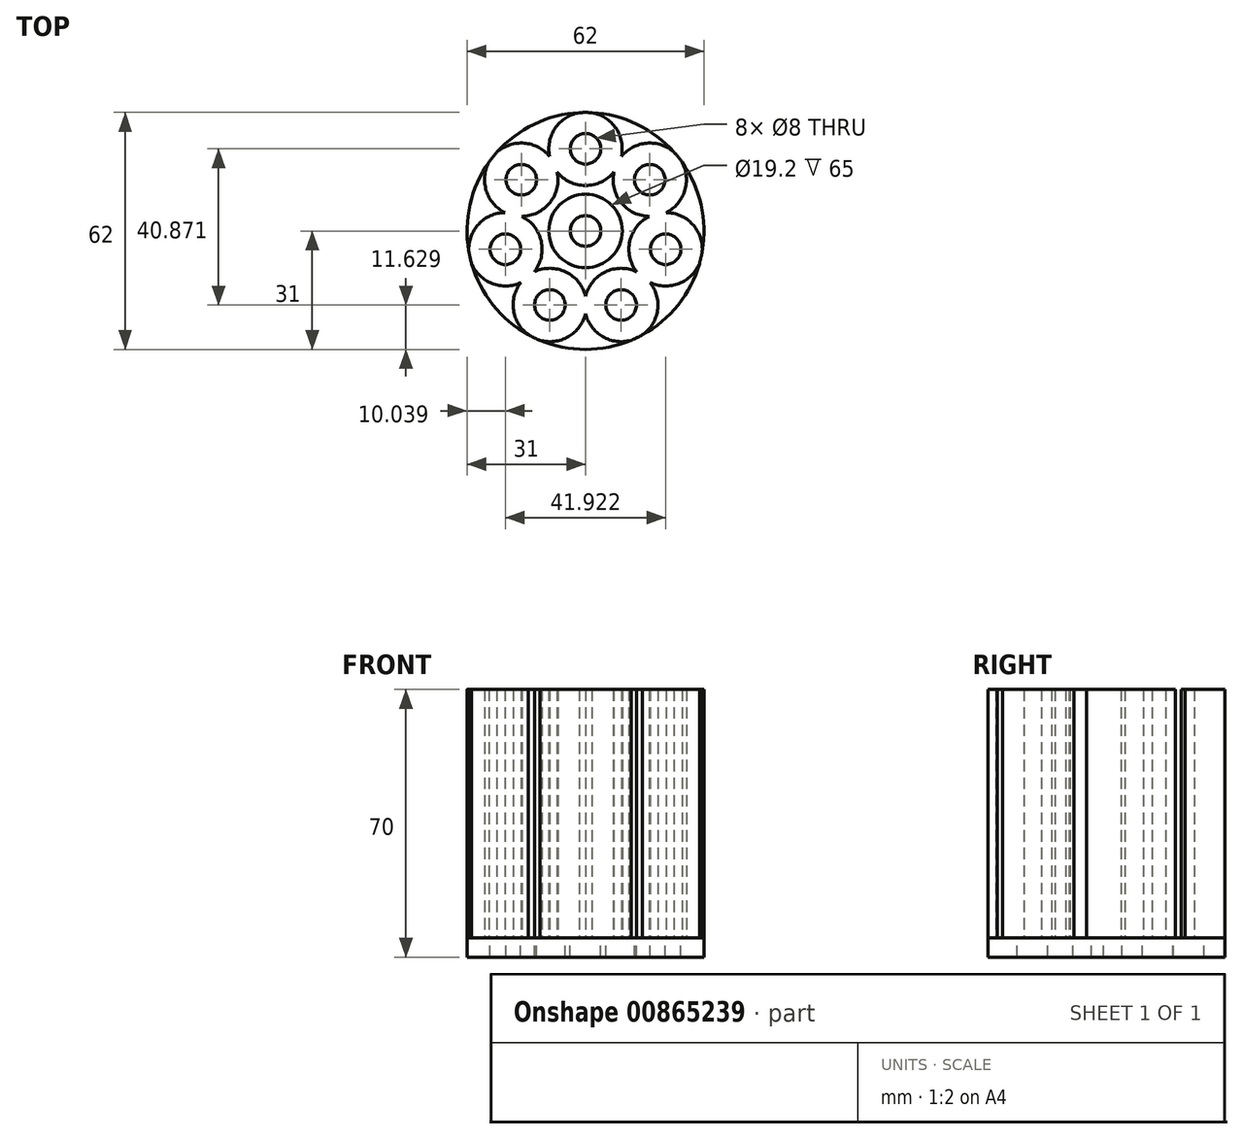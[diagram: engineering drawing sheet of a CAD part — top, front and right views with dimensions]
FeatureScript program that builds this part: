
annotation { "Feature Type Name" : "Feature", "Feature Type Description" : "" }
export const myFeature = defineFeature(function(context is Context, id is Id, definition is map)
    precondition{}
    {
        {
            var Q0;
            Q0=qCreatedBy(makeId("Top.planeOp"),FACE);
            var sketch = newSketch(context, id + "F0", { "sketchPlane" : qUnion([Q0])});
            skArc(sketch, "E0", {"start": v(-11.94, -28.6) * mm, "mid": v(0, -31) * mm, "end": v(11.94, -28.6) * mm});
            skArc(sketch, "E1", {"start": v(-7.42, 15.41) * mm, "mid": v(0, 11.9) * mm, "end": v(7.42, 15.41) * mm});
            skArc(sketch, "E2.1.0", {"start": v(-9.39, 19.5) * mm, "mid": v(-16.04, 22.97) * mm, "end": v(-23.17, 20.6) * mm});
            skArc(sketch, "E2.2.0", {"start": v(-21.1, 4.81) * mm, "mid": v(-27.97, 1.78) * mm, "end": v(-30.55, -5.27) * mm});
            skArc(sketch, "E2.3.0", {"start": v(-16.92, -13.5) * mm, "mid": v(-18.83, -20.75) * mm, "end": v(-14.93, -27.17) * mm});
            skArc(sketch, "E2.4.0", {"start": v(0, -21.64) * mm, "mid": v(4.49, -27.66) * mm, "end": v(11.94, -28.6) * mm});
            skArc(sketch, "E2.5.0", {"start": v(16.92, -13.5) * mm, "mid": v(24.42, -13.74) * mm, "end": v(29.81, -8.5) * mm});
            skArc(sketch, "E2.6.0", {"start": v(21.1, 4.81) * mm, "mid": v(25.97, 10.53) * mm, "end": v(25.24, 18) * mm});
            skCircle(sketch, "E3", {"center": v(0, 0) * mm, "radius": 9.6 * mm});
            skArc(sketch, "E4.trimOffspring", {"start": v(-16.68, 3.8) * mm, "mid": v(-9.3, 7.42) * mm, "end": v(-7.42, 15.41) * mm});
            skArc(sketch, "E5.trimOffspring", {"start": v(-13.37, -10.66) * mm, "mid": v(-11.6, -2.65) * mm, "end": v(-16.68, 3.8) * mm});
            skArc(sketch, "E6.trimOffspring", {"start": v(0, -17.1) * mm, "mid": v(-5.16, -10.72) * mm, "end": v(-13.37, -10.66) * mm});
            skArc(sketch, "E7.trimOffspring", {"start": v(13.37, -10.66) * mm, "mid": v(5.16, -10.72) * mm, "end": v(0, -17.1) * mm});
            skArc(sketch, "E8.trimOffspring", {"start": v(16.68, 3.8) * mm, "mid": v(11.6, -2.65) * mm, "end": v(13.37, -10.66) * mm});
            skArc(sketch, "E9.trimOffspring", {"start": v(9.39, 19.5) * mm, "mid": v(7.96, 26.87) * mm, "end": v(1.66, 30.96) * mm});
            skArc(sketch, "E10.trimOffspring", {"start": v(7.42, 15.41) * mm, "mid": v(9.3, 7.42) * mm, "end": v(16.68, 3.8) * mm});
            skArc(sketch, "E11.trimOffspring", {"start": v(-11.94, -28.6) * mm, "mid": v(-4.49, -27.66) * mm, "end": v(0, -21.64) * mm});
            skArc(sketch, "E12.trimOffspring", {"start": v(14.93, -27.17) * mm, "mid": v(24.24, -19.33) * mm, "end": v(29.81, -8.5) * mm});
            skArc(sketch, "E13.trimOffspring", {"start": v(14.93, -27.17) * mm, "mid": v(18.83, -20.75) * mm, "end": v(16.92, -13.5) * mm});
            skArc(sketch, "E14.trimOffspring", {"start": v(30.55, -5.27) * mm, "mid": v(30.22, 6.9) * mm, "end": v(25.24, 18) * mm});
            skArc(sketch, "E15.trimOffspring", {"start": v(30.55, -5.27) * mm, "mid": v(27.97, 1.78) * mm, "end": v(21.1, 4.81) * mm});
            skArc(sketch, "E16.trimOffspring", {"start": v(23.17, 20.6) * mm, "mid": v(16.04, 22.97) * mm, "end": v(9.39, 19.5) * mm});
            skArc(sketch, "E17.trimOffspring", {"start": v(23.17, 20.6) * mm, "mid": v(13.45, 27.93) * mm, "end": v(1.66, 30.96) * mm});
            skArc(sketch, "E18.trimOffspring", {"start": v(-1.66, 30.96) * mm, "mid": v(-7.96, 26.87) * mm, "end": v(-9.39, 19.5) * mm});
            skArc(sketch, "E19.trimOffspring", {"start": v(-1.66, 30.96) * mm, "mid": v(-13.45, 27.93) * mm, "end": v(-23.17, 20.6) * mm});
            skArc(sketch, "E20.trimOffspring", {"start": v(-25.24, 18) * mm, "mid": v(-25.97, 10.53) * mm, "end": v(-21.1, 4.81) * mm});
            skArc(sketch, "E21.trimOffspring", {"start": v(-25.24, 18) * mm, "mid": v(-30.22, 6.9) * mm, "end": v(-30.55, -5.27) * mm});
            skArc(sketch, "E22.trimOffspring", {"start": v(-29.81, -8.5) * mm, "mid": v(-24.24, -19.33) * mm, "end": v(-14.93, -27.17) * mm});
            skArc(sketch, "E23.trimOffspring", {"start": v(-29.81, -8.5) * mm, "mid": v(-24.42, -13.74) * mm, "end": v(-16.92, -13.5) * mm});
            skSolve(sketch);
        }
        {
            var Q0;
            Q0 = qSketchRegion(id + "F0", true);
            extrude(context, id + "F1", {"entities" : qUnion([Q0]), "depth" : 65 * mm, "offsetDistance" : 25 * mm});
        }
        {
            var Q0;
            Q0=makeQuery(id+"F1.opExtrude","CAP_FACE",FACE,{"disambiguationData":[OSD([sQuery(id+"F0.wireOp",EDGE,"E1"),sQuery(id+"F0.wireOp",EDGE,"E3"),sQuery(id+"F0.wireOp",EDGE,"E4.trimOffspring"),sQuery(id+"F0.wireOp",EDGE,"E5.trimOffspring"),sQuery(id+"F0.wireOp",EDGE,"E6.trimOffspring"),sQuery(id+"F0.wireOp",EDGE,"E7.trimOffspring"),sQuery(id+"F0.wireOp",EDGE,"E8.trimOffspring"),sQuery(id+"F0.wireOp",EDGE,"E10.trimOffspring")])],"isStart":true});
            var sketch = newSketch(context, id + "F2", { "sketchPlane" : qUnion([Q0])});
            skCircle(sketch, "E24", {"center": v(0, 0) * mm, "radius": 31 * mm});
            skSolve(sketch);
        }
        {
            var Q0;
            Q0=makeQuery(id+"F2.imprint","IMPRINT",FACE,{"disambiguationData":[TD([[makeQuery(id+"F2.imprint","IMPRINT",EDGE,{"derivedFrom":sQuery(id+"F2.wireOp",EDGE,"E24")}),1.0]])]});
            var Q1;
            Q1=makeQuery(id+"F2.imprint","IMPRINT",FACE,{"disambiguationData":[TD([[makeQuery(id+"F2.imprint","IMPRINT",EDGE,{"derivedFrom":makeQuery(id+"F1.opExtrude","CAP_EDGE",EDGE,{"disambiguationData":[OSD([sQuery(id+"F0.wireOp",EDGE,"E1")])],"isStart":true})}),1.0]])]});
            var Q2;
            Q2=makeQuery(id+"F2.imprint","IMPRINT",FACE,{"disambiguationData":[TD([[makeQuery(id+"F2.imprint","IMPRINT",EDGE,{"derivedFrom":makeQuery(id+"F1.opExtrude","CAP_EDGE",EDGE,{"disambiguationData":[OSD([sQuery(id+"F0.wireOp",EDGE,"E3")])],"isStart":true})}),-1.0]])]});
            extrude(context, id + "F3", {"entities" : qUnion([Q0, Q1, Q2]), "depth" : 5 * mm, "offsetDistance" : 25 * mm});
        }
        {
            var Q0;
            Q0=makeQuery(id+"F3.opExtrude","CAP_FACE",FACE,{"disambiguationData":[OSD([sQuery(id+"F2.wireOp",EDGE,"E24")])],"isStart":true});
            var sketch = newSketch(context, id + "F4", { "sketchPlane" : qUnion([Q0])});
            skArc(sketch, "E25.0.0", {"start": v(16.92, -13.5) * mm, "mid": v(18.83, -20.75) * mm, "end": v(14.93, -27.17) * mm});
            skArc(sketch, "E25.0.2", {"start": v(14.93, -27.17) * mm, "mid": v(18.83, -20.75) * mm, "end": v(16.92, -13.5) * mm});
            skPoint(sketch, "E26.0", {"position": v(27.97, 1.78) * mm});
            skArc(sketch, "E27.0", {"start": v(30.55, -5.27) * mm, "mid": v(27.97, 1.78) * mm, "end": v(21.1, 4.81) * mm});
            skArc(sketch, "E28.0", {"start": v(23.17, 20.6) * mm, "mid": v(16.04, 22.97) * mm, "end": v(9.39, 19.5) * mm});
            skArc(sketch, "E29.0", {"start": v(-1.66, 30.96) * mm, "mid": v(-7.96, 26.87) * mm, "end": v(-9.39, 19.5) * mm});
            skArc(sketch, "E30.0", {"start": v(-9.39, 19.5) * mm, "mid": v(-16.04, 22.97) * mm, "end": v(-23.17, 20.6) * mm});
            skArc(sketch, "E31.0", {"start": v(-21.1, 4.81) * mm, "mid": v(-27.97, 1.78) * mm, "end": v(-30.55, -5.27) * mm});
            skArc(sketch, "E32.0", {"start": v(-16.92, -13.5) * mm, "mid": v(-18.83, -20.75) * mm, "end": v(-14.93, -27.17) * mm});
            skCircle(sketch, "E33.0", {"center": v(0, 0) * mm, "radius": 9.6 * mm});
            skSolve(sketch);
        }
        {
            var Q0;
            Q0=sQuery(id+"F4.wireOp",VERTEX,"E25.0.0.center");
            var Q1;
            Q1=sQuery(id+"F4.wireOp",VERTEX,"E27.0.center");
            var Q2;
            Q2=sQuery(id+"F4.wireOp",VERTEX,"E28.0.center");
            var Q3;
            Q3=sQuery(id+"F4.wireOp",VERTEX,"E29.0.center");
            var Q4;
            Q4=sQuery(id+"F4.wireOp",VERTEX,"E33.0.center");
            var Q5;
            Q5=sQuery(id+"F4.wireOp",VERTEX,"E30.0.center");
            var Q6;
            Q6=sQuery(id+"F4.wireOp",VERTEX,"E31.0.center");
            var Q7;
            Q7=sQuery(id+"F4.wireOp",VERTEX,"E32.0.center");
            var Q8;
            Q8=makeQuery(id+"F3.opExtrude","SWEPT_BODY",BODY,{"disambiguationData":[OSD([sQuery(id+"F2.wireOp",EDGE,"E24")])]});
            hole(context, id + "F5", {"style" : HoleStyle.SIMPLE, "endStyle" : HoleEndStyle.THROUGH, "holeDiameter" : 8 * mm, "majorDiameter" : 5 * mm, "isTappedThrough" : true, "tappedDepth" : 12 * mm, "tapClearance" : 3, "locations" : qUnion([Q0, Q1, Q2, Q3, Q4, Q5, Q6, Q7]), "scope" : qUnion([Q8])});
        }
    });
